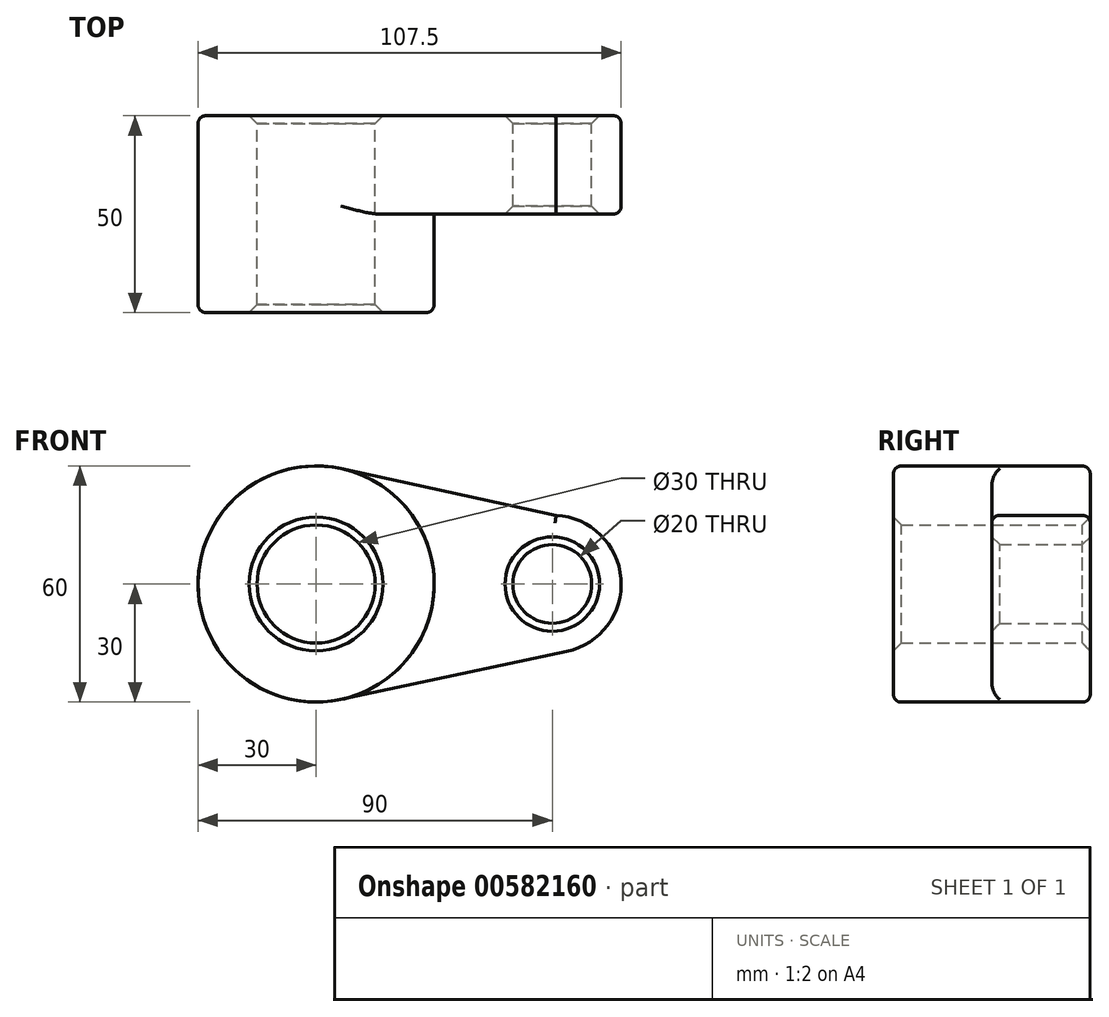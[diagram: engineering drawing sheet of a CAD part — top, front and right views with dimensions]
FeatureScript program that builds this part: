
annotation { "Feature Type Name" : "Feature", "Feature Type Description" : "" }
export const myFeature = defineFeature(function(context is Context, id is Id, definition is map)
    precondition{}
    {
        {
            var Q0;
            Q0=qCreatedBy(makeId("Front.planeOp"),FACE);
            var sketch = newSketch(context, id + "F0", { "sketchPlane" : qUnion([Q0])});
            skCircle(sketch, "E0", {"center": v(0, 0) * mm, "radius": 30 * mm});
            skCircle(sketch, "E1", {"center": v(60, 0) * mm, "radius": 17.5 * mm});
            skLineSegment(sketch, "E2", {"start": v(6.36, 29.32) * mm, "end": v(66.36, 16.3) * mm});
            skLineSegment(sketch, "E3", {"start": v(6.25, -29.34) * mm, "end": v(66.36, -16.54) * mm});
            skCircle(sketch, "E4", {"center": v(0, 0) * mm, "radius": 15 * mm});
            skCircle(sketch, "E5", {"center": v(60, 0) * mm, "radius": 10 * mm});
            skSolve(sketch);
        }
        {
            var Q0;
            Q0 = qSketchRegion(id + "F0", true);
            extrude(context, id + "F1", {"entities" : qUnion([Q0]), "depth" : 25 * mm, "offsetDistance" : 25 * mm});
        }
        {
            var Q0;
            Q0=makeQuery(id+"F0.imprint","IMPRINT",FACE,{"disambiguationData":[TD([[makeQuery(id+"F0.imprint","IMPRINT",EDGE,{"derivedFrom":sQuery(id+"F0.wireOp",EDGE,"E4")}),-1.0]])]});
            extrude(context, id + "F2", {"entities" : qUnion([Q0]), "operationType" : NewBodyOperationType.ADD, "depth" : 50 * mm, "offsetDistance" : 25 * mm});
        }
        {
            var Q0;
            Q0=makeQuery(id+"F2.opExtrude","CAP_EDGE",EDGE,{"disambiguationData":[OSD([sQuery(id+"F0.wireOp",EDGE,"E0")])],"isStart":false});
            var Q1;
            Q1=makeQuery(id+"F1.opExtrude","CAP_EDGE",EDGE,{"disambiguationData":[OSD([sQuery(id+"F0.wireOp",EDGE,"E3")])],"isStart":true});
            var Q2;
            Q2=makeQuery(id+"F1.opExtrude","CAP_EDGE",EDGE,{"disambiguationData":[OSD([sQuery(id+"F0.wireOp",EDGE,"E3")])],"isStart":false});
            var Q3;
            Q3=makeQuery(id+"F1.opExtrude","CAP_EDGE",EDGE,{"disambiguationData":[OSD([sQuery(id+"F0.wireOp",EDGE,"E1")])],"isStart":false});
            var Q4;
            Q4=makeQuery(id+"F1.opExtrude","CAP_EDGE",EDGE,{"disambiguationData":[OSD([sQuery(id+"F0.wireOp",EDGE,"E2")])],"isStart":false});
            var Q5;
            Q5=makeQuery(id+"F1.opExtrude","CAP_EDGE",EDGE,{"disambiguationData":[OSD([sQuery(id+"F0.wireOp",EDGE,"E1")])],"isStart":true});
            var Q6;
            Q6=makeQuery(id+"F1.opExtrude","CAP_EDGE",EDGE,{"disambiguationData":[OSD([sQuery(id+"F0.wireOp",EDGE,"E0")])],"isStart":true});
            var Q7;
            Q7=makeQuery(id+"F1.opExtrude","CAP_EDGE",EDGE,{"disambiguationData":[OSD([sQuery(id+"F0.wireOp",EDGE,"E2")])],"isStart":true});
            fillet(context, id + "F3", {"entities" : qUnion([Q0, Q1, Q2, Q3, Q4, Q5, Q6, Q7]), "radius" : 2 * mm, "tangentPropagation" : true, "allowEdgeOverflow" : false});
        }
        {
            var Q0;
            Q0=makeQuery(id+"F2.opExtrude","CAP_EDGE",EDGE,{"disambiguationData":[OSD([sQuery(id+"F0.wireOp",EDGE,"E4")])],"isStart":false});
            var Q1;
            Q1=makeQuery(id+"F1.opExtrude","CAP_EDGE",EDGE,{"disambiguationData":[OSD([sQuery(id+"F0.wireOp",EDGE,"E5")])],"isStart":false});
            var Q2;
            Q2=makeQuery(id+"F1.opExtrude","CAP_EDGE",EDGE,{"disambiguationData":[OSD([sQuery(id+"F0.wireOp",EDGE,"E4")])],"isStart":true});
            var Q3;
            Q3=makeQuery(id+"F1.opExtrude","CAP_EDGE",EDGE,{"disambiguationData":[OSD([sQuery(id+"F0.wireOp",EDGE,"E5")])],"isStart":true});
            chamfer(context, id + "F4", {"entities" : qUnion([Q0, Q1, Q2, Q3]), "width" : 2 * mm, "tangentPropagation" : true});
        }
    });
